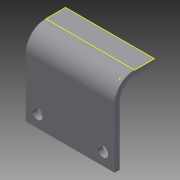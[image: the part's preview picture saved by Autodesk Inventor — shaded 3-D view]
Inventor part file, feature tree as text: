
AUTODESK INVENTOR PART (.ipt)
format: ipt  version: 2013 (Build 170138000, 138)  size: 117,248 bytes
history: native  units: in
note: dims shown in document units (in); Inventor stores cm internally (conversion verified against a paired STEP export)
features: sketch x6, sheet_metal_op x4, other x2
ambient origin geometry x8: Origin, YZ Plane, XZ Plane, XY Plane, X Axis, Y Axis, Z Axis, Center Point
bodies: Solid1 (feature_tree)
feature tree (12):
  sheet_metal_op  "Face1"
  sheet_metal_op  "Flange1"
  sketch  "Sketch3"  dims[d3=0.295in]
  sketch  "Sketch4"  dims[d4=1.181in]
  sketch  "Sketch5"  dims[d5=0.295in]
  sketch  "Sketch6"  dims[d6=0.26in d7=0.26in d8=0.125in d9=0.125in d10=0.0625in d11=0.25in d12=0.125in d13=1.0in d14=90.0deg d15=0.375in d16=0.5in d17=0.125in d18=0.125in]
  sketch  "Sketch1"  dims[d1=2.244in]
  other  "Plate1"
  sketch  "Sketch2"  dims[d2=1.5in]
  other  "Plate2"
  sheet_metal_op  "Bend1"
  sheet_metal_op  "Corner1"
